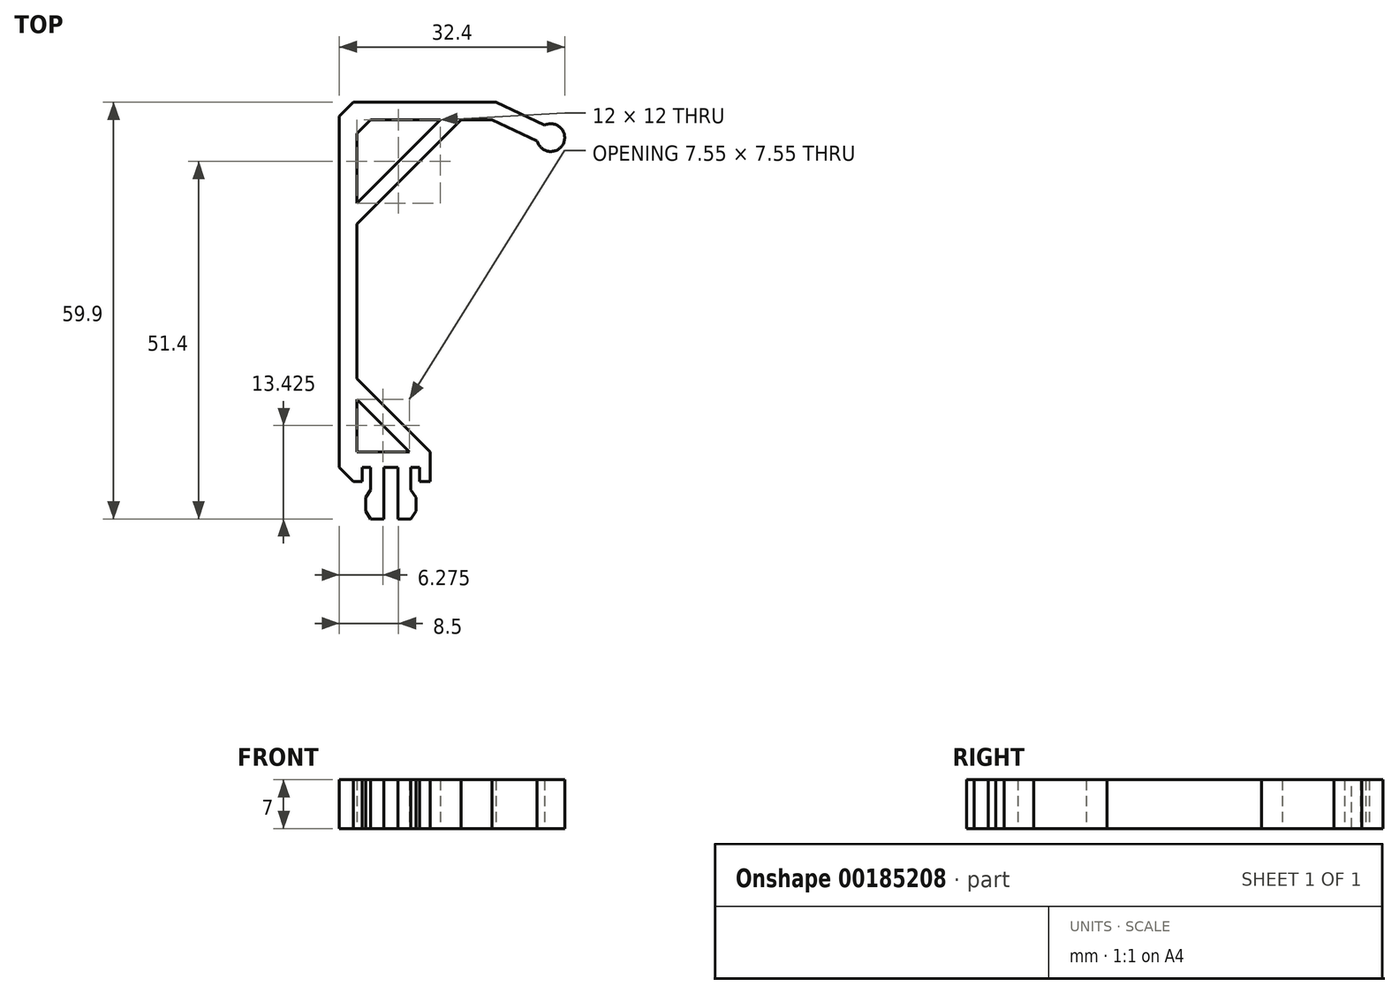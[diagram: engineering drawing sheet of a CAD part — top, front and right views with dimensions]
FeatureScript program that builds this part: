
annotation { "Feature Type Name" : "Feature", "Feature Type Description" : "" }
export const myFeature = defineFeature(function(context is Context, id is Id, definition is map)
    precondition{}
    {
        {
            var Q0;
            Q0=qCreatedBy(makeId("Top.planeOp"),FACE);
            var sketch = newSketch(context, id + "F0", { "sketchPlane" : qUnion([Q0])});
            skLineSegment(sketch, "E0.bottom", {"start": v(-1, 0) * mm, "end": v(-2.9, 0) * mm});
            skLineSegment(sketch, "E0.top", {"start": v(-1, -7.4) * mm, "end": v(-2.9, -7.4) * mm});
            skLineSegment(sketch, "E0.left", {"start": v(-1, 0) * mm, "end": v(-1, -7.4) * mm});
            skLineSegment(sketch, "E0.right", {"start": v(-2.9, 0) * mm, "end": v(-2.9, -7.4) * mm});
            skLineSegment(sketch, "E1", {"start": v(-2.9, -7.4) * mm, "end": v(-3.6, -6.3) * mm});
            skLineSegment(sketch, "E2", {"start": v(-3.6, -6.3) * mm, "end": v(-3.6, -4.3) * mm});
            skLineSegment(sketch, "E3", {"start": v(-3.6, -4.3) * mm, "end": v(-2.9, -3.2) * mm});
            skLineSegment(sketch, "E4.MirrorCS", {"start": v(1, 0) * mm, "end": v(2.9, 0) * mm});
            skLineSegment(sketch, "E5.MirrorCS", {"start": v(3.6, -4.3) * mm, "end": v(2.9, -3.2) * mm});
            skLineSegment(sketch, "E6.MirrorCS", {"start": v(1, -7.4) * mm, "end": v(2.9, -7.4) * mm});
            skLineSegment(sketch, "E7.MirrorCS", {"start": v(1, 0) * mm, "end": v(1, -7.4) * mm});
            skLineSegment(sketch, "E8.MirrorCS", {"start": v(2.9, 0) * mm, "end": v(2.9, -7.4) * mm});
            skLineSegment(sketch, "E9.MirrorCS", {"start": v(2.9, -7.4) * mm, "end": v(3.6, -6.3) * mm});
            skLineSegment(sketch, "E10.MirrorCS", {"start": v(3.6, -6.3) * mm, "end": v(3.6, -4.3) * mm});
            skLineSegment(sketch, "E11", {"start": v(1, 0) * mm, "end": v(-1, 0) * mm});
            skLineSegment(sketch, "E12", {"start": v(2.9, 0) * mm, "end": v(4.15, 0) * mm});
            skLineSegment(sketch, "E13", {"start": v(4.15, 0) * mm, "end": v(4.15, -2) * mm});
            skLineSegment(sketch, "E14", {"start": v(4.15, -2) * mm, "end": v(5.65, -2) * mm});
            skLineSegment(sketch, "E15", {"start": v(5.65, -2) * mm, "end": v(5.65, 2.25) * mm});
            skLineSegment(sketch, "E16", {"start": v(2.65, 2.25) * mm, "end": v(-4.9, 2.25) * mm});
            skLineSegment(sketch, "E17", {"start": v(-2.9, 0) * mm, "end": v(-4.15, 0) * mm});
            skLineSegment(sketch, "E18", {"start": v(-4.15, 0) * mm, "end": v(-4.15, -2) * mm});
            skLineSegment(sketch, "E19", {"start": v(-4.15, -2) * mm, "end": v(-7.4, -2) * mm});
            skLineSegment(sketch, "E20", {"start": v(-7.4, -2) * mm, "end": v(-7.4, 52.5) * mm});
            skLineSegment(sketch, "E21", {"start": v(-4.9, 2.25) * mm, "end": v(-4.9, 9.8) * mm});
            skLineSegment(sketch, "E22", {"start": v(-4.9, 50) * mm, "end": v(14.55, 50) * mm});
            skLineSegment(sketch, "E23", {"start": v(5.65, 2.25) * mm, "end": v(-4.9, 12.8) * mm});
            skLineSegment(sketch, "E24", {"start": v(2.65, 2.25) * mm, "end": v(-4.9, 9.8) * mm});
            skLineSegment(sketch, "E25.trimOffspring", {"start": v(-4.9, 12.8) * mm, "end": v(-4.9, 50) * mm});
            skLineSegment(sketch, "E26", {"start": v(-4.9, 38) * mm, "end": v(7.1, 50) * mm});
            skLineSegment(sketch, "E27", {"start": v(10.1, 50) * mm, "end": v(-4.9, 35) * mm});
            skLineSegment(sketch, "E28", {"start": v(14.55, 50) * mm, "end": v(22.48, 46.3) * mm});
            skLineSegment(sketch, "E29", {"start": v(22.48, 46.3) * mm, "end": v(23.53, 48.57) * mm});
            skLineSegment(sketch, "E30", {"start": v(23.53, 48.57) * mm, "end": v(15.1, 52.5) * mm});
            skLineSegment(sketch, "E31", {"start": v(15.1, 52.5) * mm, "end": v(-7.4, 52.5) * mm});
            skCircle(sketch, "E32", {"center": v(23, 47.43) * mm, "radius": 2 * mm});
            skSolve(sketch);
        }
        {
            var Q0;
            Q0=qSketchRegion(id+"F0",true);
            extrude(context, id + "F1", {"entities" : qUnion([Q0]), "depth" : 7 * mm});
        }
        {
            var Q0;
            Q0=makeQuery(id+"F1.opExtrude","SWEPT_EDGE",EDGE,{"disambiguationData":[OSD([sQuery(id+"F0.wireOp",EDGE,"E20"),sQuery(id+"F0.wireOp",EDGE,"0dllHYmb-7COt-ttak-97sy-ixv086gSsBnm")])]});
            var Q1;
            Q1=makeQuery(id+"F1.opExtrude","SWEPT_EDGE",EDGE,{"disambiguationData":[OSD([sQuery(id+"F0.wireOp",EDGE,"E22"),sQuery(id+"F0.wireOp",EDGE,"E25.trimOffspring")])]});
            chamfer(context, id + "F2", {"entities" : qUnion([Q0, Q1]), "width" : 2 * mm, "tangentPropagation" : true});
        }
    });
